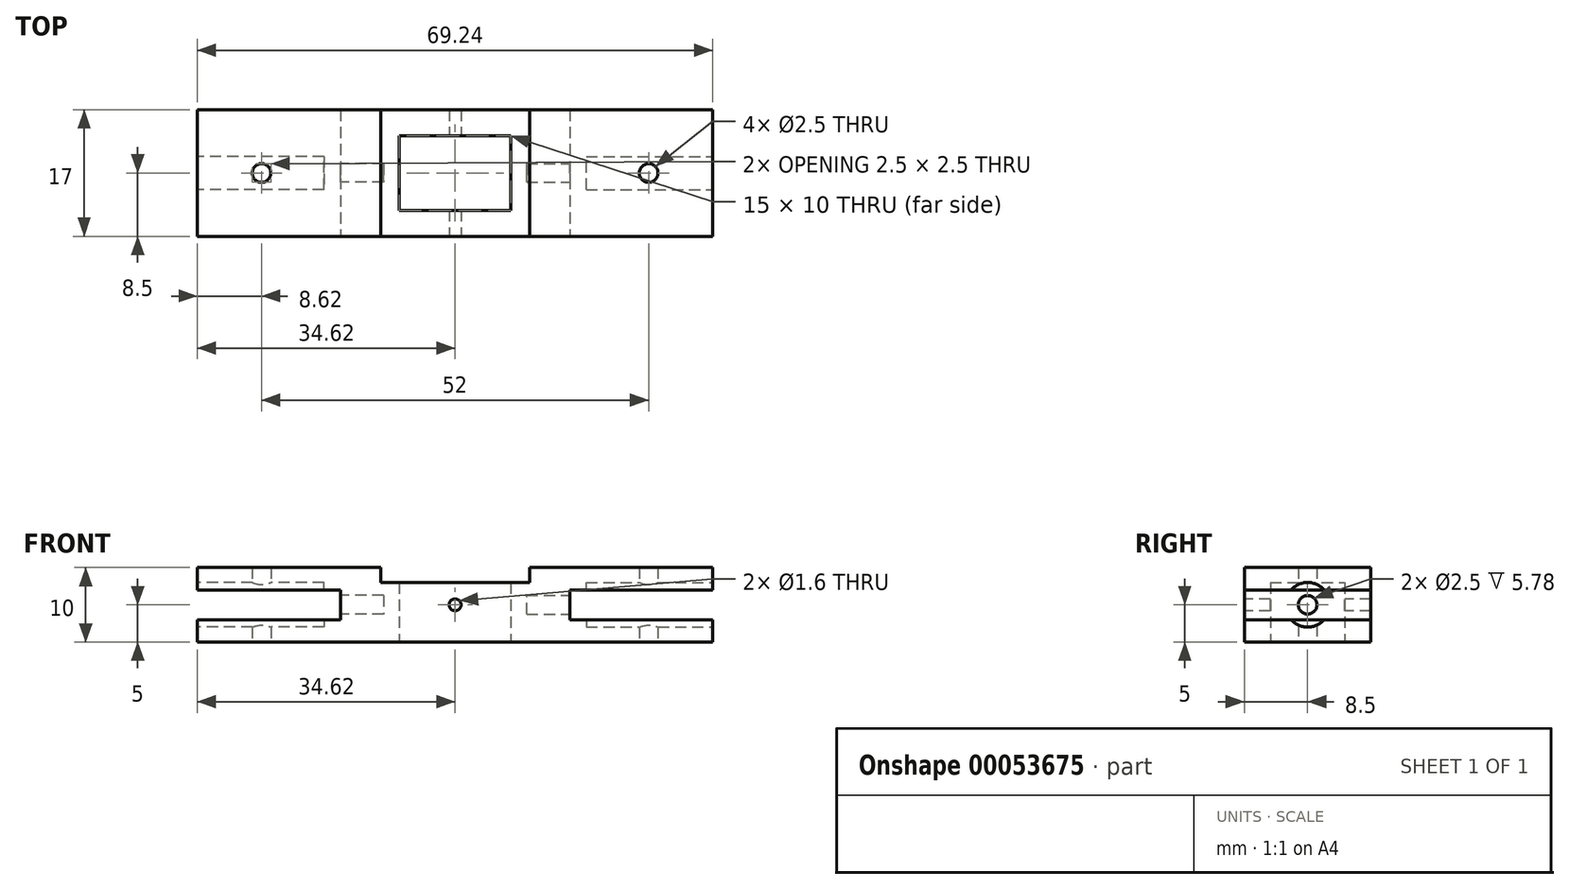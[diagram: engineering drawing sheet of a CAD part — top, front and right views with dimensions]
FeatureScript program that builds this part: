
annotation { "Feature Type Name" : "Feature", "Feature Type Description" : "" }
export const myFeature = defineFeature(function(context is Context, id is Id, definition is map)
    precondition{}
    {
        {
            var Q0;
            Q0=qCreatedBy(makeId("Top.planeOp"),FACE);
            var sketch = newSketch(context, id + "F0", { "sketchPlane" : qUnion([Q0])});
            skLineSegment(sketch, "E0.rect.bottom", {"start": v(7.5, -5) * mm, "end": v(-7.5, -5) * mm});
            skLineSegment(sketch, "E0.rect.top", {"start": v(7.5, 5) * mm, "end": v(-7.5, 5) * mm});
            skLineSegment(sketch, "E0.rect.left", {"start": v(7.5, -5) * mm, "end": v(7.5, 5) * mm});
            skLineSegment(sketch, "E0.rect.right", {"start": v(-7.5, -5) * mm, "end": v(-7.5, 5) * mm});
            skPoint(sketch, "E0.rect.middle", {"position": v(0, 0) * mm});
            skLineSegment(sketch, "E1.rect.bottom", {"start": v(18, -1.25) * mm, "end": v(-18, -1.25) * mm, "construction": true});
            skLineSegment(sketch, "E1.rect.top", {"start": v(18, 1.25) * mm, "end": v(-18, 1.25) * mm, "construction": true});
            skLineSegment(sketch, "E1.rect.left", {"start": v(18, -1.25) * mm, "end": v(18, 1.25) * mm, "construction": true});
            skLineSegment(sketch, "E1.rect.right", {"start": v(-18, -1.25) * mm, "end": v(-18, 1.25) * mm, "construction": true});
            skCircle(sketch, "E2", {"center": v(-26, 0) * mm, "radius": 1.25 * mm});
            skCircle(sketch, "E3.MirrorC", {"center": v(26, 0) * mm, "radius": 1.25 * mm});
            skLineSegment(sketch, "E4.rect.bottom", {"start": v(34.62, -8.5) * mm, "end": v(-34.62, -8.5) * mm});
            skLineSegment(sketch, "E4.rect.top", {"start": v(34.62, 8.5) * mm, "end": v(-34.62, 8.5) * mm});
            skLineSegment(sketch, "E4.rect.left", {"start": v(34.62, -8.5) * mm, "end": v(34.62, 8.5) * mm});
            skLineSegment(sketch, "E4.rect.right", {"start": v(-34.62, -8.5) * mm, "end": v(-34.62, 8.5) * mm});
            skSolve(sketch);
        }
        {
            var Q0;
            Q0 = qSketchRegion(id + "F0", true);
            extrude(context, id + "F1", {"entities" : qUnion([Q0]), "endBound" : BoundingType.SYMMETRIC, "depth" : 10 * mm});
        }
        {
            var Q0;
            Q0=makeQuery(id+"F1.opExtrude","SWEPT_FACE",FACE,{"disambiguationData":[OSD([sQuery(id+"F0.wireOp",EDGE,"E4.rect.bottom")])]});
            var sketch = newSketch(context, id + "F2", { "sketchPlane" : qUnion([Q0])});
            skCircle(sketch, "E5", {"center": v(0, 0) * mm, "radius": 0.8 * mm});
            skLineSegment(sketch, "E6.rect.bottom", {"start": v(-34.62, 2) * mm, "end": v(-15.4, 2) * mm});
            skLineSegment(sketch, "E6.rect.top", {"start": v(-34.62, -2) * mm, "end": v(-15.4, -2) * mm});
            skLineSegment(sketch, "E6.rect.left", {"start": v(-34.62, 2) * mm, "end": v(-34.62, -2) * mm});
            skLineSegment(sketch, "E6.rect.right", {"start": v(-15.4, 2) * mm, "end": v(-15.4, -2) * mm});
            skPoint(sketch, "E6.rect.middle", {"position": v(-25, 0) * mm});
            skLineSegment(sketch, "E7.MirrorCS", {"start": v(34.62, 2) * mm, "end": v(15.4, 2) * mm});
            skLineSegment(sketch, "E8.MirrorCS", {"start": v(34.62, 2) * mm, "end": v(34.62, -2) * mm});
            skLineSegment(sketch, "E9.MirrorCS", {"start": v(34.62, -2) * mm, "end": v(15.4, -2) * mm});
            skLineSegment(sketch, "E10.MirrorCS", {"start": v(15.4, 2) * mm, "end": v(15.4, -2) * mm});
            skLineSegment(sketch, "E11.rect.bottom", {"start": v(15.4, 1.25) * mm, "end": v(-15.4, 1.25) * mm, "construction": true});
            skLineSegment(sketch, "E11.rect.top", {"start": v(15.4, -1.25) * mm, "end": v(-15.4, -1.25) * mm, "construction": true});
            skLineSegment(sketch, "E11.rect.left", {"start": v(15.4, 1.25) * mm, "end": v(15.4, -1.25) * mm, "construction": true});
            skLineSegment(sketch, "E11.rect.right", {"start": v(-15.4, 1.25) * mm, "end": v(-15.4, -1.25) * mm, "construction": true});
            skLineSegment(sketch, "E12.rect.bottom", {"start": v(-15.4, 3) * mm, "end": v(-12.8, 3) * mm, "construction": true});
            skLineSegment(sketch, "E12.rect.top", {"start": v(-15.4, -3) * mm, "end": v(-12.8, -3) * mm, "construction": true});
            skLineSegment(sketch, "E12.rect.left", {"start": v(-15.4, 3) * mm, "end": v(-15.4, -3) * mm, "construction": true});
            skLineSegment(sketch, "E12.rect.right", {"start": v(-12.8, 3) * mm, "end": v(-12.8, -3) * mm, "construction": true});
            skPoint(sketch, "E12.rect.middle", {"position": v(-14.1, 0) * mm});
            skSolve(sketch);
        }
        {
            var Q0;
            Q0 = qSketchRegion(id + "F2", true);
            extrude(context, id + "F3", {"entities" : qUnion([Q0]), "operationType" : NewBodyOperationType.REMOVE, "oppositeDirection" : true, "depth" : 25 * mm});
        }
        {
            var Q0;
            {var subQ0=sQuery(id+"F0.wireOp",EDGE,"E4.rect.right");Q0=makeQuery(id+"F3.boolean.opBoolean","SPLIT",FACE,{"disambiguationData":[TD([makeQuery(id+"F3.opExtrude","SWEPT_FACE",FACE,{"disambiguationData":[OSD([sQuery(id+"F2.wireOp",EDGE,"E6.rect.bottom")])]})])],"derivedFrom":makeQuery(id+"F1.opExtrude","SWEPT_FACE",FACE,{"disambiguationData":[OSD([subQ0])]})});}
            var sketch = newSketch(context, id + "F4", { "sketchPlane" : qUnion([Q0])});
            skCircle(sketch, "E13", {"center": v(0, 0) * mm, "radius": 1.25 * mm});
            skSolve(sketch);
        }
        {
            var Q0;
            Q0 = qSketchRegion(id + "F4", true);
            extrude(context, id + "F5", {"entities" : qUnion([Q0]), "operationType" : NewBodyOperationType.REMOVE, "oppositeDirection" : true, "depth" : 25 * mm});
        }
        {
            var Q0;
            {var subQ0=sQuery(id+"F0.wireOp",EDGE,"E4.rect.right");Q0=makeQuery(id+"F3.boolean.opBoolean","SPLIT",FACE,{"disambiguationData":[TD([makeQuery(id+"F3.opExtrude","SWEPT_FACE",FACE,{"disambiguationData":[OSD([sQuery(id+"F2.wireOp",EDGE,"E6.rect.bottom")])]})])],"derivedFrom":makeQuery(id+"F1.opExtrude","SWEPT_FACE",FACE,{"disambiguationData":[OSD([subQ0])]})});}
            var sketch = newSketch(context, id + "F6", { "sketchPlane" : qUnion([Q0])});
            skCircle(sketch, "E14", {"center": v(0, 0) * mm, "radius": 3 * mm});
            skSolve(sketch);
        }
        {
            var Q0;
            Q0 = qSketchRegion(id + "F6", true);
            extrude(context, id + "F7", {"entities" : qUnion([Q0]), "operationType" : NewBodyOperationType.REMOVE, "oppositeDirection" : true, "depth" : 17 * mm});
        }
        {
            var Q0;
            {var subQ0=sQuery(id+"F0.wireOp",EDGE,"E4.rect.left");Q0=makeQuery(id+"F3.boolean.opBoolean","SPLIT",FACE,{"disambiguationData":[TD([makeQuery(id+"F3.opExtrude","SWEPT_FACE",FACE,{"disambiguationData":[OSD([sQuery(id+"F2.wireOp",EDGE,"E7.MirrorCS")])]})])],"derivedFrom":makeQuery(id+"F1.opExtrude","SWEPT_FACE",FACE,{"disambiguationData":[OSD([subQ0])]})});}
            var sketch = newSketch(context, id + "F8", { "sketchPlane" : qUnion([Q0])});
            skCircle(sketch, "E15", {"center": v(0, 0) * mm, "radius": 1.25 * mm});
            skSolve(sketch);
        }
        {
            var Q0;
            Q0 = qSketchRegion(id + "F8", true);
            extrude(context, id + "F9", {"entities" : qUnion([Q0]), "operationType" : NewBodyOperationType.REMOVE, "oppositeDirection" : true, "depth" : 25 * mm});
        }
        {
            var Q0;
            {var subQ0=sQuery(id+"F0.wireOp",EDGE,"E4.rect.left");Q0=makeQuery(id+"F3.boolean.opBoolean","SPLIT",FACE,{"disambiguationData":[TD([makeQuery(id+"F3.opExtrude","SWEPT_FACE",FACE,{"disambiguationData":[OSD([sQuery(id+"F2.wireOp",EDGE,"E7.MirrorCS")])]})])],"derivedFrom":makeQuery(id+"F1.opExtrude","SWEPT_FACE",FACE,{"disambiguationData":[OSD([subQ0])]})});}
            var sketch = newSketch(context, id + "F10", { "sketchPlane" : qUnion([Q0])});
            skCircle(sketch, "E16", {"center": v(0, 0) * mm, "radius": 3 * mm});
            skSolve(sketch);
        }
        {
            var Q0;
            Q0 = qSketchRegion(id + "F10", true);
            extrude(context, id + "F11", {"entities" : qUnion([Q0]), "operationType" : NewBodyOperationType.REMOVE, "oppositeDirection" : true, "depth" : 17 * mm});
        }
        {
            var Q0;
            Q0=makeQuery(id+"F1.opExtrude","CAP_FACE",FACE,{"disambiguationData":[OSD([sQuery(id+"F0.wireOp",EDGE,"E0.rect.bottom"),sQuery(id+"F0.wireOp",EDGE,"E0.rect.top"),sQuery(id+"F0.wireOp",EDGE,"E0.rect.left"),sQuery(id+"F0.wireOp",EDGE,"E0.rect.right"),sQuery(id+"F0.wireOp",EDGE,"E2"),sQuery(id+"F0.wireOp",EDGE,"E3.MirrorC"),sQuery(id+"F0.wireOp",EDGE,"E4.rect.bottom"),sQuery(id+"F0.wireOp",EDGE,"E4.rect.top"),sQuery(id+"F0.wireOp",EDGE,"E4.rect.left"),sQuery(id+"F0.wireOp",EDGE,"E4.rect.right")])],"isStart":false});
            var sketch = newSketch(context, id + "F12", { "sketchPlane" : qUnion([Q0])});
            skLineSegment(sketch, "E17.rect.bottom", {"start": v(-10, 8.5) * mm, "end": v(10, 8.5) * mm});
            skLineSegment(sketch, "E17.rect.top", {"start": v(-10, -8.5) * mm, "end": v(10, -8.5) * mm});
            skLineSegment(sketch, "E17.rect.left", {"start": v(-10, 8.5) * mm, "end": v(-10, -8.5) * mm});
            skLineSegment(sketch, "E17.rect.right", {"start": v(10, 8.5) * mm, "end": v(10, -8.5) * mm});
            skPoint(sketch, "E17.rect.middle", {"position": v(0, 0) * mm});
            skSolve(sketch);
        }
        {
            var Q0;
            Q0 = qSketchRegion(id + "F12", true);
            extrude(context, id + "F13", {"entities" : qUnion([Q0]), "operationType" : NewBodyOperationType.REMOVE, "oppositeDirection" : true, "depth" : 2 * mm});
        }
    });
